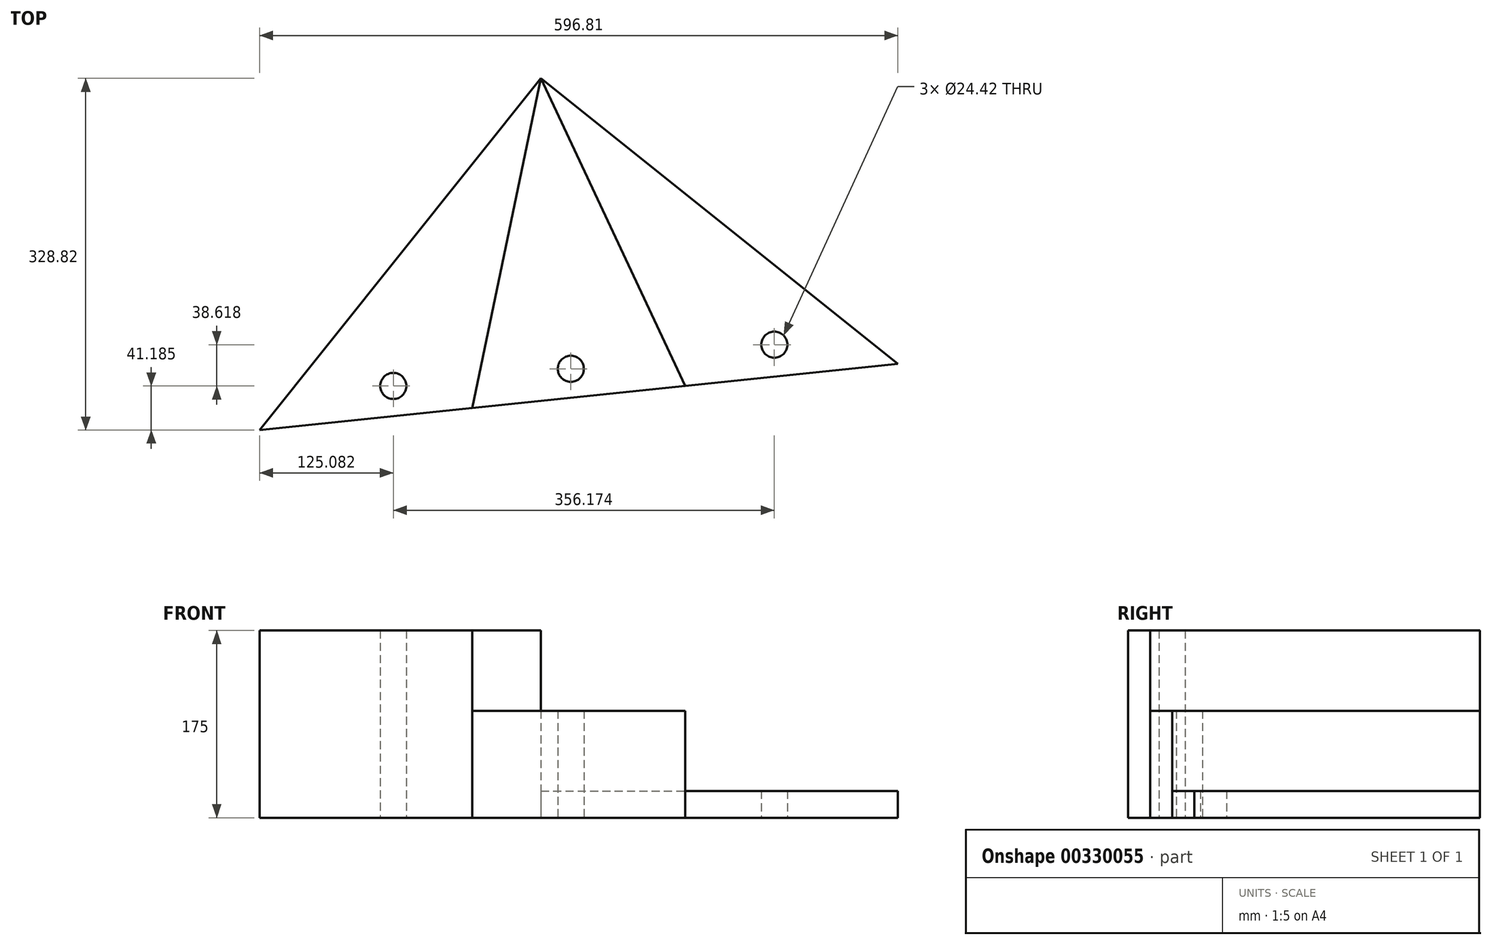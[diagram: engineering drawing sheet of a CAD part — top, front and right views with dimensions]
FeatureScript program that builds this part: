
annotation { "Feature Type Name" : "Feature", "Feature Type Description" : "" }
export const myFeature = defineFeature(function(context is Context, id is Id, definition is map)
    precondition{}
    {
        {
            var Q0;
            Q0=qCreatedBy(makeId("Top.planeOp"),FACE);
            var sketch = newSketch(context, id + "F0", { "sketchPlane" : qUnion([Q0])});
            skLineSegment(sketch, "E0", {"start": v(-147.14, 290.77) * mm, "end": v(-410.2, -38.05) * mm});
            skLineSegment(sketch, "E1", {"start": v(-410.2, -38.05) * mm, "end": v(186.6, 23.77) * mm});
            skLineSegment(sketch, "E2", {"start": v(-147.14, 290.77) * mm, "end": v(186.6, 23.77) * mm});
            skLineSegment(sketch, "E3", {"start": v(-147.14, 290.77) * mm, "end": v(-211.26, -17.44) * mm});
            skLineSegment(sketch, "E4", {"start": v(-147.14, 290.77) * mm, "end": v(-12.33, 3.16) * mm});
            skCircle(sketch, "E5", {"center": v(-119.2, 19.17) * mm, "radius": 12.21 * mm});
            skCircle(sketch, "E6", {"center": v(71.06, 41.75) * mm, "radius": 12.21 * mm});
            skCircle(sketch, "E7", {"center": v(-285.12, 3.14) * mm, "radius": 12.21 * mm});
            skSolve(sketch);
        }
        {
            var Q0;
            {var subQ0=sQuery(id+"F0.wireOp",EDGE,"E0");Q0=makeQuery(id+"F0.imprint","IMPRINT",FACE,{"disambiguationData":[TD([[makeQuery(id+"F0.imprint","IMPRINT",EDGE,{"derivedFrom":subQ0}),1.0]])]});}
            extrude(context, id + "F1", {"entities" : qUnion([Q0]), "depth" : 175 * mm});
        }
        {
            var Q0;
            {var subQ0=sQuery(id+"F0.wireOp",EDGE,"E2");Q0=makeQuery(id+"F0.imprint","IMPRINT",FACE,{"disambiguationData":[TD([[makeQuery(id+"F0.imprint","IMPRINT",EDGE,{"derivedFrom":subQ0}),-1.0]])]});}
            extrude(context, id + "F2", {"entities" : qUnion([Q0]), "depth" : 25 * mm});
        }
        {
            var Q0;
            {var subQ0=sQuery(id+"F0.wireOp",EDGE,"E3");Q0=makeQuery(id+"F0.imprint","IMPRINT",FACE,{"disambiguationData":[TD([[makeQuery(id+"F0.imprint","IMPRINT",EDGE,{"derivedFrom":subQ0}),1.0]])]});}
            extrude(context, id + "F3", {"entities" : qUnion([Q0]), "depth" : 100 * mm});
        }
    });
